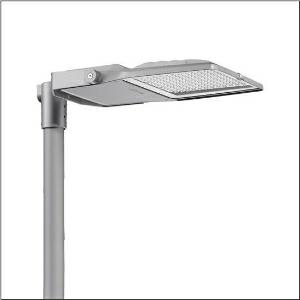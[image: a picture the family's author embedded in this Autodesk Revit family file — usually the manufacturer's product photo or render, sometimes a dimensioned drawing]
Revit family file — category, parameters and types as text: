
# Revit family: floodlight_fl_21_midi___pl64_5xa7785f2e3a_d9f8
name_source: partatom
category: Lighting Fixtures
units: mm (PartAtom-declared; Revit-internal decimal feet)

## family parameters
Cut with Voids When Loaded = No
Host = Face
Light Source = No
Part Type = Normal
Room Calculation Point = No
Round Connector Dimension = Use Diameter
Shared = No

## types (1)
- --- (1 x LED, 34530 lm, 271.6 W, 3000K)
    Apparent Load = 272 VA
    CIE Flux Codes = 28 80 98 100 100
    Color Rendering = 70
    Color Temperature = 3000K
    Default Elevation = 1800 mm
    Description = Floodlight FL 21 midi, floodlight, primary light control with lens, of PMMA, primary optical cover: protective disc, of toughened safety glass, transparent, light distribution: PL64, light emission: direct distribution, installation type: surface-mounted, LED, High Power LED, rated luminous flux: 34.530lm, luminous efficacy: 127lm/W, light colour: 730, colour temperature: 3000K, control gear: Smart Interface (Zhaga), control: flexible luminous flux parameterisation, time-dependent luminous flux control, constant luminous flux control, overheat protection, pre-setting: logarithmic dimming characteristic, with terminal, 6-pole, mains connection: 220..240V, AC, 50/60Hz, start of lifetime: 272W, end of service life: 287W, reduction: 123W, luminaire housing, of diecast aluminium, powder-coated, SITECO metallic grey (DB 702S), corrosivity category C5 mid according to DIN EN ISO 12944, suitable for swimming pools, chlorine-resistant, sealing non-destructively replaceable, please order mast flange separately, mast bracket, of steel, galvanised, powder-coated, SITECO metallic grey (DB 702S), Smart Interface above, protection rating (complete): IP66, insulation class (complete): insulation class II (safety insulation), certification: CE, ENEC, VDE, protection symbol: D, impact resistance: IK08, permissible operating ambient temperature: -40..+40°C, permissible operating ambient temperature for outdoor applications: -40..+50°C, standard: DIN EN 12944, LABS conformity tested according to VDMA 24364:2018-05, packaging unit: 1 piece

Light Distribution: PL64
    Height = 76 mm
    Lamp = 1 x LED
    Lamp Light Flux = 34530 lm
    Lamp Power = 271.6 W
    Lamp count = 1
    Length = 657 mm
    Luminous efficacy = 127 lm/W
    Manufacturer = Siteco
    ModVariant = No
    Model = 5XA7785F2E3A
    Number of Poles = 1
    OnlyDefault = Yes
    Power Factor = 1
    Product Name = Floodlight FL 21 midi | PL64
    Product group = floodlight | pylon annexe
    ProductGroupID = 6201
    Protection Class = Protection class II
    Protection Degree = IP 66
    RLX_Detail_Level = 1
    RLX_Emergency_Light_Flux = 0 lm
    RLX_Emergency_Type = 0
    RLX_Emergency_Type_DB = No
    RlxData = <blob elided: 153609 chars, md5=2e2fef15>
    Socket = socket
    Standby Power = 0 W
    System Light Flux = 34530 lm
    System Power = 272 W
    Type Comments = factory setting: luminous flux: 100 % | dim-lin: 254 | 620 mA
    Type Image = l_1007123.jpg
    URL = http://relux.com
    VarID = @adj_179009
    Voltage = 0 V
    Weight = 0.00 kg
    Width = 442 mm

## geometry (parser evidence)
native form markers: Blend x4, Sweep x14
no freeform markers — native parametric forms only
